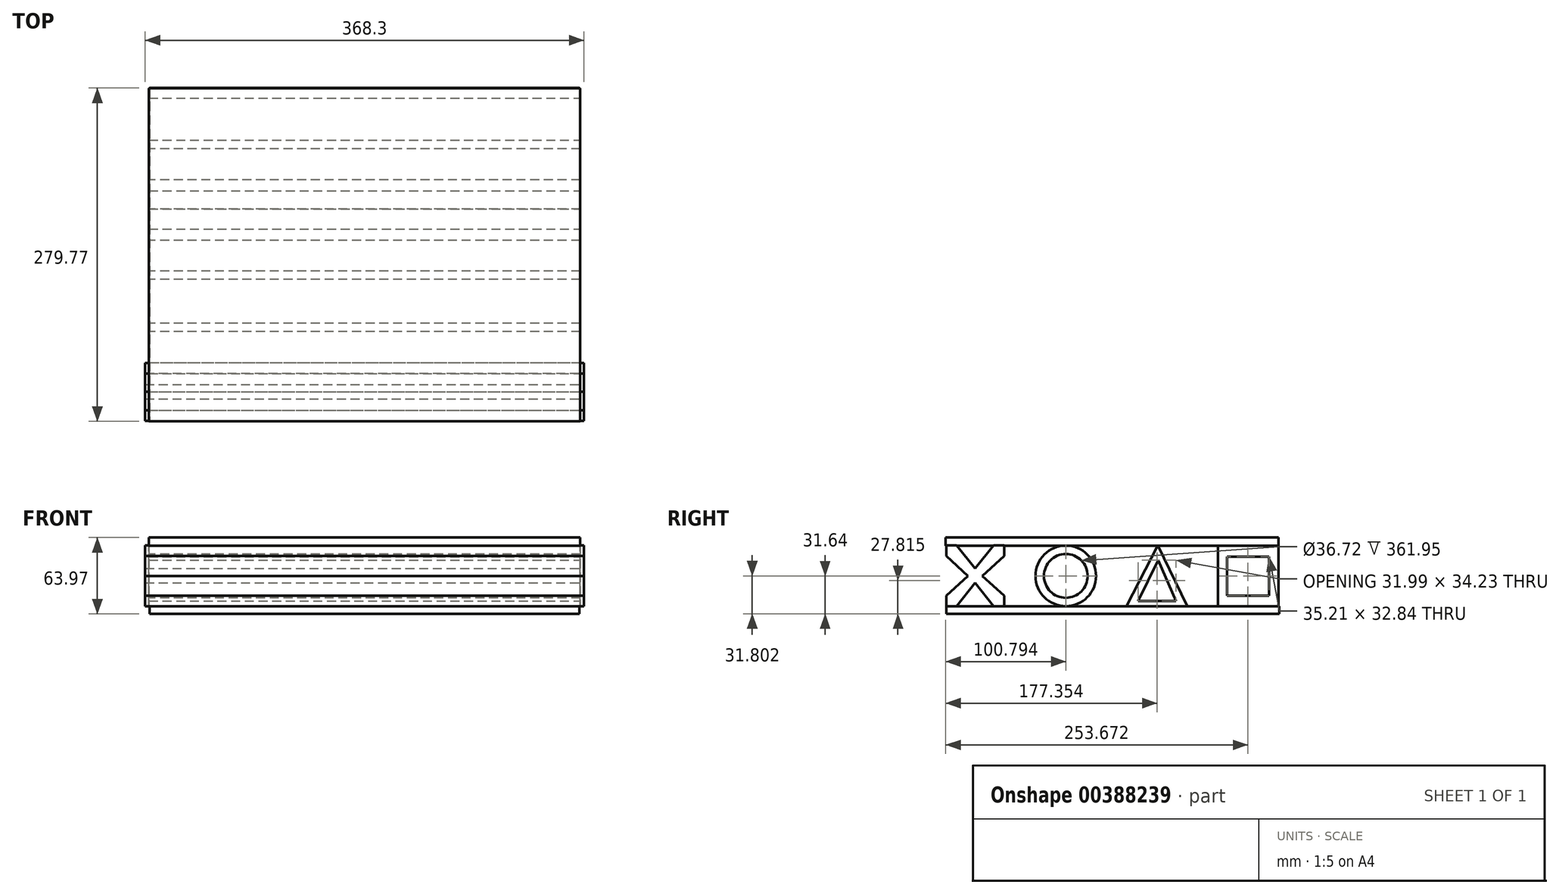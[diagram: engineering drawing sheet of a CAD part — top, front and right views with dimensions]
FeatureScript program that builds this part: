
annotation { "Feature Type Name" : "Feature", "Feature Type Description" : "" }
export const myFeature = defineFeature(function(context is Context, id is Id, definition is map)
    precondition{}
    {
        {
            var Q0;
            Q0=qCreatedBy(makeId("Top.planeOp"),FACE);
            var sketch = newSketch(context, id + "F0", { "sketchPlane" : qUnion([Q0])});
            skLineSegment(sketch, "E0.bottom", {"start": v(-180.34, 139.7) * mm, "end": v(180.34, 139.7) * mm});
            skLineSegment(sketch, "E0.top", {"start": v(-180.34, -139.7) * mm, "end": v(180.34, -139.7) * mm});
            skLineSegment(sketch, "E0.left", {"start": v(-180.34, 139.7) * mm, "end": v(-180.34, -139.7) * mm});
            skLineSegment(sketch, "E0.right", {"start": v(180.34, 139.7) * mm, "end": v(180.34, -139.7) * mm});
            skPoint(sketch, "E0.middle", {"position": v(0, 0) * mm});
            skSolve(sketch);
        }
        {
            var Q0;
            Q0 = qSketchRegion(id + "F0", true);
            extrude(context, id + "F1", {"entities" : qUnion([Q0]), "depth" : 6.35 * mm});
        }
        {
            var Q0;
            Q0=qCreatedBy(makeId("Right.planeOp"),FACE);
            var sketch = newSketch(context, id + "F2", { "sketchPlane" : qUnion([Q0])});
            skLineSegment(sketch, "E1.bottom", {"start": v(139.34, 6.3) * mm, "end": v(88.54, 6.3) * mm});
            skLineSegment(sketch, "E1.top", {"start": v(139.34, 57.1) * mm, "end": v(88.54, 57.1) * mm});
            skLineSegment(sketch, "E1.left", {"start": v(139.34, 6.3) * mm, "end": v(139.34, 57.1) * mm});
            skLineSegment(sketch, "E1.right", {"start": v(88.54, 6.3) * mm, "end": v(88.54, 57.1) * mm});
            skSolve(sketch);
        }
        {
            var Q0;
            Q0=makeQuery(id+"F2.imprint","IMPRINT",FACE,{"disambiguationData":[TD([[makeQuery(id+"F2.imprint","IMPRINT",EDGE,{"derivedFrom":sQuery(id+"F2.wireOp",EDGE,"E1.bottom")}),-1.0]])]});
            extrude(context, id + "F3", {"entities" : qUnion([Q0]), "endBound" : BoundingType.SYMMETRIC, "depth" : 361.95 * mm});
        }
        {
            var Q0;
            Q0=qCreatedBy(makeId("Right.planeOp"),FACE);
            var sketch = newSketch(context, id + "F4", { "sketchPlane" : qUnion([Q0])});
            skLineSegment(sketch, "E2", {"start": v(11.68, 6.37) * mm, "end": v(38.05, 57.6) * mm});
            skLineSegment(sketch, "E3", {"start": v(38.05, 57.6) * mm, "end": v(62.72, 6.35) * mm});
            skLineSegment(sketch, "E4", {"start": v(62.72, 6.35) * mm, "end": v(11.68, 6.37) * mm});
            skSolve(sketch);
        }
        {
            var Q0;
            Q0=makeQuery(id+"F4.imprint","IMPRINT",FACE,{"disambiguationData":[TD([[makeQuery(id+"F4.imprint","IMPRINT",EDGE,{"derivedFrom":sQuery(id+"F4.wireOp",EDGE,"E2")}),-1.0]])]});
            extrude(context, id + "F5", {"entities" : qUnion([Q0]), "endBound" : BoundingType.SYMMETRIC, "depth" : 361.95 * mm});
        }
        {
            var Q0;
            Q0=qCreatedBy(makeId("Right.planeOp"),FACE);
            var sketch = newSketch(context, id + "F6", { "sketchPlane" : qUnion([Q0])});
            skLineSegment(sketch, "E5.bottom", {"start": v(96, 15.22) * mm, "end": v(131.2, 15.22) * mm});
            skLineSegment(sketch, "E5.top", {"start": v(96, 48.06) * mm, "end": v(131.2, 48.06) * mm});
            skLineSegment(sketch, "E5.left", {"start": v(96, 15.22) * mm, "end": v(96, 48.06) * mm});
            skLineSegment(sketch, "E5.right", {"start": v(131.2, 15.22) * mm, "end": v(131.2, 48.06) * mm});
            skPoint(sketch, "E5.middle", {"position": v(113.6, 31.64) * mm});
            skSolve(sketch);
        }
        {
            var Q0;
            Q0 = qSketchRegion(id + "F6", true);
            extrude(context, id + "F7", {"entities" : qUnion([Q0]), "operationType" : NewBodyOperationType.REMOVE, "endBound" : BoundingType.SYMMETRIC, "oppositeDirection" : true, "depth" : 361.95 * mm});
        }
        {
            var Q0;
            Q0=qCreatedBy(makeId("Right.planeOp"),FACE);
            var sketch = newSketch(context, id + "F8", { "sketchPlane" : qUnion([Q0])});
            skLineSegment(sketch, "E6", {"start": v(38.1, 44.93) * mm, "end": v(53.28, 10.7) * mm});
            skLineSegment(sketch, "E7", {"start": v(53.28, 10.7) * mm, "end": v(21.29, 10.7) * mm});
            skLineSegment(sketch, "E8", {"start": v(21.29, 10.7) * mm, "end": v(38.1, 44.93) * mm});
            skSolve(sketch);
        }
        {
            var Q0;
            Q0 = qSketchRegion(id + "F8", true);
            extrude(context, id + "F9", {"entities" : qUnion([Q0]), "operationType" : NewBodyOperationType.REMOVE, "endBound" : BoundingType.SYMMETRIC, "oppositeDirection" : true, "depth" : 361.95 * mm});
        }
        {
            var Q0;
            Q0=qCreatedBy(makeId("Right.planeOp"),FACE);
            var sketch = newSketch(context, id + "F10", { "sketchPlane" : qUnion([Q0])});
            skCircle(sketch, "E9", {"center": v(-39.29, 31.8) * mm, "radius": 25.41 * mm});
            skSolve(sketch);
        }
        {
            var Q0;
            Q0=qCreatedBy(makeId("Right.planeOp"),FACE);
            var sketch = newSketch(context, id + "F11", { "sketchPlane" : qUnion([Q0])});
            skCircle(sketch, "E10", {"center": v(-39.28, 31.8) * mm, "radius": 18.36 * mm});
            skSolve(sketch);
        }
        {
            var Q0;
            Q0=makeQuery(id+"F10.imprint","IMPRINT",FACE,{"disambiguationData":[TD([[makeQuery(id+"F10.imprint","IMPRINT",EDGE,{"derivedFrom":sQuery(id+"F10.wireOp",EDGE,"E9")}),1.0]])]});
            extrude(context, id + "F12", {"entities" : qUnion([Q0]), "endBound" : BoundingType.SYMMETRIC, "depth" : 361.95 * mm});
        }
        {
            var Q0;
            Q0 = qSketchRegion(id + "F11", true);
            extrude(context, id + "F13", {"entities" : qUnion([Q0]), "operationType" : NewBodyOperationType.REMOVE, "endBound" : BoundingType.SYMMETRIC, "depth" : 361.95 * mm});
        }
        {
            var Q0;
            Q0=qCreatedBy(makeId("Right.planeOp"),FACE);
            var sketch = newSketch(context, id + "F14", { "sketchPlane" : qUnion([Q0])});
            skLineSegment(sketch, "E11.bottom", {"start": v(-139.64, 6.38) * mm, "end": v(-91, 6.38) * mm});
            skLineSegment(sketch, "E11.top", {"start": v(-139.64, 57.37) * mm, "end": v(-91, 57.37) * mm});
            skLineSegment(sketch, "E11.left", {"start": v(-139.64, 6.38) * mm, "end": v(-139.64, 57.37) * mm});
            skLineSegment(sketch, "E11.right", {"start": v(-91, 6.38) * mm, "end": v(-91, 57.37) * mm});
            skPoint(sketch, "E11.middle", {"position": v(-115.32, 31.88) * mm});
            skSolve(sketch);
        }
        {
            var Q0;
            Q0=makeQuery(id+"F14.imprint","IMPRINT",FACE,{"disambiguationData":[TD([[makeQuery(id+"F14.imprint","IMPRINT",EDGE,{"derivedFrom":sQuery(id+"F14.wireOp",EDGE,"E11.bottom")}),1.0]])]});
            extrude(context, id + "F15", {"entities" : qUnion([Q0]), "endBound" : BoundingType.SYMMETRIC, "depth" : 368.3 * mm});
        }
        {
            var Q0;
            Q0=makeQuery(id+"F15.opExtrude","CAP_FACE",FACE,{"disambiguationData":[OSD([sQuery(id+"F14.wireOp",EDGE,"E11.bottom"),sQuery(id+"F14.wireOp",EDGE,"E11.top"),sQuery(id+"F14.wireOp",EDGE,"E11.left"),sQuery(id+"F14.wireOp",EDGE,"E11.right")])],"isStart":true});
            var sketch = newSketch(context, id + "F16", { "sketchPlane" : qUnion([Q0])});
            skLineSegment(sketch, "E12", {"start": v(99.8, 57.37) * mm, "end": v(115.34, 37.95) * mm});
            skLineSegment(sketch, "E13", {"start": v(115.34, 37.95) * mm, "end": v(130.89, 57.37) * mm});
            skLineSegment(sketch, "E14", {"start": v(130.89, 57.37) * mm, "end": v(99.8, 57.37) * mm});
            skSolve(sketch);
        }
        {
            var Q0;
            Q0=makeQuery(id+"F16.imprint","IMPRINT",FACE,{"disambiguationData":[TD([[makeQuery(id+"F16.imprint","IMPRINT",EDGE,{"derivedFrom":sQuery(id+"F16.wireOp",EDGE,"E12")}),1.0]])]});
            extrude(context, id + "F17", {"entities" : qUnion([Q0]), "operationType" : NewBodyOperationType.REMOVE, "endBound" : BoundingType.SYMMETRIC, "depth" : 736.6 * mm});
        }
        {
            var Q0;
            Q0=makeQuery(id+"F15.opExtrude","CAP_FACE",FACE,{"disambiguationData":[OSD([sQuery(id+"F14.wireOp",EDGE,"E11.bottom"),sQuery(id+"F14.wireOp",EDGE,"E11.top"),sQuery(id+"F14.wireOp",EDGE,"E11.left"),sQuery(id+"F14.wireOp",EDGE,"E11.right")])],"isStart":true});
            var sketch = newSketch(context, id + "F18", { "sketchPlane" : qUnion([Q0])});
            skLineSegment(sketch, "E15.bottom", {"start": v(109.28, 37.95) * mm, "end": v(121.35, 37.95) * mm});
            skLineSegment(sketch, "E15.top", {"start": v(109.28, 25.91) * mm, "end": v(121.35, 25.91) * mm});
            skLineSegment(sketch, "E15.left", {"start": v(109.28, 37.95) * mm, "end": v(109.28, 25.91) * mm});
            skLineSegment(sketch, "E15.right", {"start": v(121.35, 37.95) * mm, "end": v(121.35, 25.91) * mm});
            skPoint(sketch, "E15.middle", {"position": v(115.31, 31.93) * mm});
            skSolve(sketch);
        }
        {
            var Q0;
            Q0=makeQuery(id+"F18.imprint","IMPRINT",FACE,{"disambiguationData":[TD([[makeQuery(id+"F18.imprint","IMPRINT",EDGE,{"derivedFrom":sQuery(id+"F18.wireOp",EDGE,"E15.top")}),-1.0]])]});
            var sketch = newSketch(context, id + "F19", { "sketchPlane" : qUnion([Q0])});
            skLineSegment(sketch, "E16", {"start": v(99.65, 6.31) * mm, "end": v(115.34, 25.86) * mm});
            skLineSegment(sketch, "E17", {"start": v(115.34, 25.86) * mm, "end": v(131.03, 6.2) * mm});
            skLineSegment(sketch, "E18", {"start": v(131.03, 6.2) * mm, "end": v(99.65, 6.31) * mm});
            skSolve(sketch);
        }
        {
            var Q0;
            Q0=makeQuery(id+"F18.imprint","IMPRINT",FACE,{"disambiguationData":[TD([[makeQuery(id+"F18.imprint","IMPRINT",EDGE,{"derivedFrom":sQuery(id+"F18.wireOp",EDGE,"E15.top")}),-1.0]])]});
            var sketch = newSketch(context, id + "F20", { "sketchPlane" : qUnion([Q0])});
            skLineSegment(sketch, "E19", {"start": v(90.95, 48.7) * mm, "end": v(109.28, 31.87) * mm});
            skLineSegment(sketch, "E20", {"start": v(109.28, 31.87) * mm, "end": v(90.99, 15.17) * mm});
            skLineSegment(sketch, "E21", {"start": v(90.99, 15.17) * mm, "end": v(90.95, 48.7) * mm});
            skSolve(sketch);
        }
        {
            var Q0;
            Q0=makeQuery(id+"F18.imprint","IMPRINT",FACE,{"disambiguationData":[TD([[makeQuery(id+"F18.imprint","IMPRINT",EDGE,{"derivedFrom":sQuery(id+"F18.wireOp",EDGE,"E15.top")}),-1.0]])]});
            var sketch = newSketch(context, id + "F21", { "sketchPlane" : qUnion([Q0])});
            skLineSegment(sketch, "E22", {"start": v(139.62, 48.66) * mm, "end": v(121.35, 31.88) * mm});
            skLineSegment(sketch, "E23", {"start": v(121.35, 31.88) * mm, "end": v(139.7, 15.16) * mm});
            skLineSegment(sketch, "E24", {"start": v(139.7, 15.16) * mm, "end": v(139.7, 48.66) * mm});
            skLineSegment(sketch, "E25", {"start": v(139.7, 48.66) * mm, "end": v(139.7, 48.72) * mm});
            skLineSegment(sketch, "E26", {"start": v(139.7, 48.72) * mm, "end": v(139.7, 48.75) * mm});
            skLineSegment(sketch, "E27", {"start": v(139.7, 48.75) * mm, "end": v(139.62, 48.66) * mm});
            skSolve(sketch);
        }
        {
            var Q0;
            Q0 = qSketchRegion(id + "F21", true);
            extrude(context, id + "F22", {"entities" : qUnion([Q0]), "operationType" : NewBodyOperationType.REMOVE, "endBound" : BoundingType.SYMMETRIC, "depth" : 762 * mm});
        }
        {
            var Q0;
            Q0 = qSketchRegion(id + "F20", true);
            extrude(context, id + "F23", {"entities" : qUnion([Q0]), "operationType" : NewBodyOperationType.REMOVE, "endBound" : BoundingType.SYMMETRIC, "depth" : 762 * mm});
        }
        {
            var Q0;
            {var subQ0=sQuery(id+"F19.wireOp",EDGE,"E16");Q0=makeQuery(id+"F19.imprint","IMPRINT",FACE,{"disambiguationData":[TD([[makeQuery(id+"F19.imprint","IMPRINT",EDGE,{"derivedFrom":subQ0}),-1.0]])]});}
            extrude(context, id + "F24", {"entities" : qUnion([Q0]), "operationType" : NewBodyOperationType.REMOVE, "endBound" : BoundingType.SYMMETRIC, "depth" : 762 * mm});
        }
        {
            var Q0;
            Q0=qCreatedBy(makeId("Right.planeOp"),FACE);
            var sketch = newSketch(context, id + "F25", { "sketchPlane" : qUnion([Q0])});
            skLineSegment(sketch, "E28.bottom", {"start": v(139.33, 57.02) * mm, "end": v(-140.07, 57.02) * mm});
            skLineSegment(sketch, "E28.top", {"start": v(139.33, 63.97) * mm, "end": v(-140.07, 63.97) * mm});
            skLineSegment(sketch, "E28.left", {"start": v(139.33, 57.02) * mm, "end": v(139.33, 63.97) * mm});
            skLineSegment(sketch, "E28.right", {"start": v(-140.07, 57.02) * mm, "end": v(-140.07, 63.97) * mm});
            skSolve(sketch);
        }
        {
            var Q0;
            Q0 = qSketchRegion(id + "F25", true);
            extrude(context, id + "F26", {"entities" : qUnion([Q0]), "endBound" : BoundingType.SYMMETRIC, "depth" : 361.95 * mm});
        }
    });
